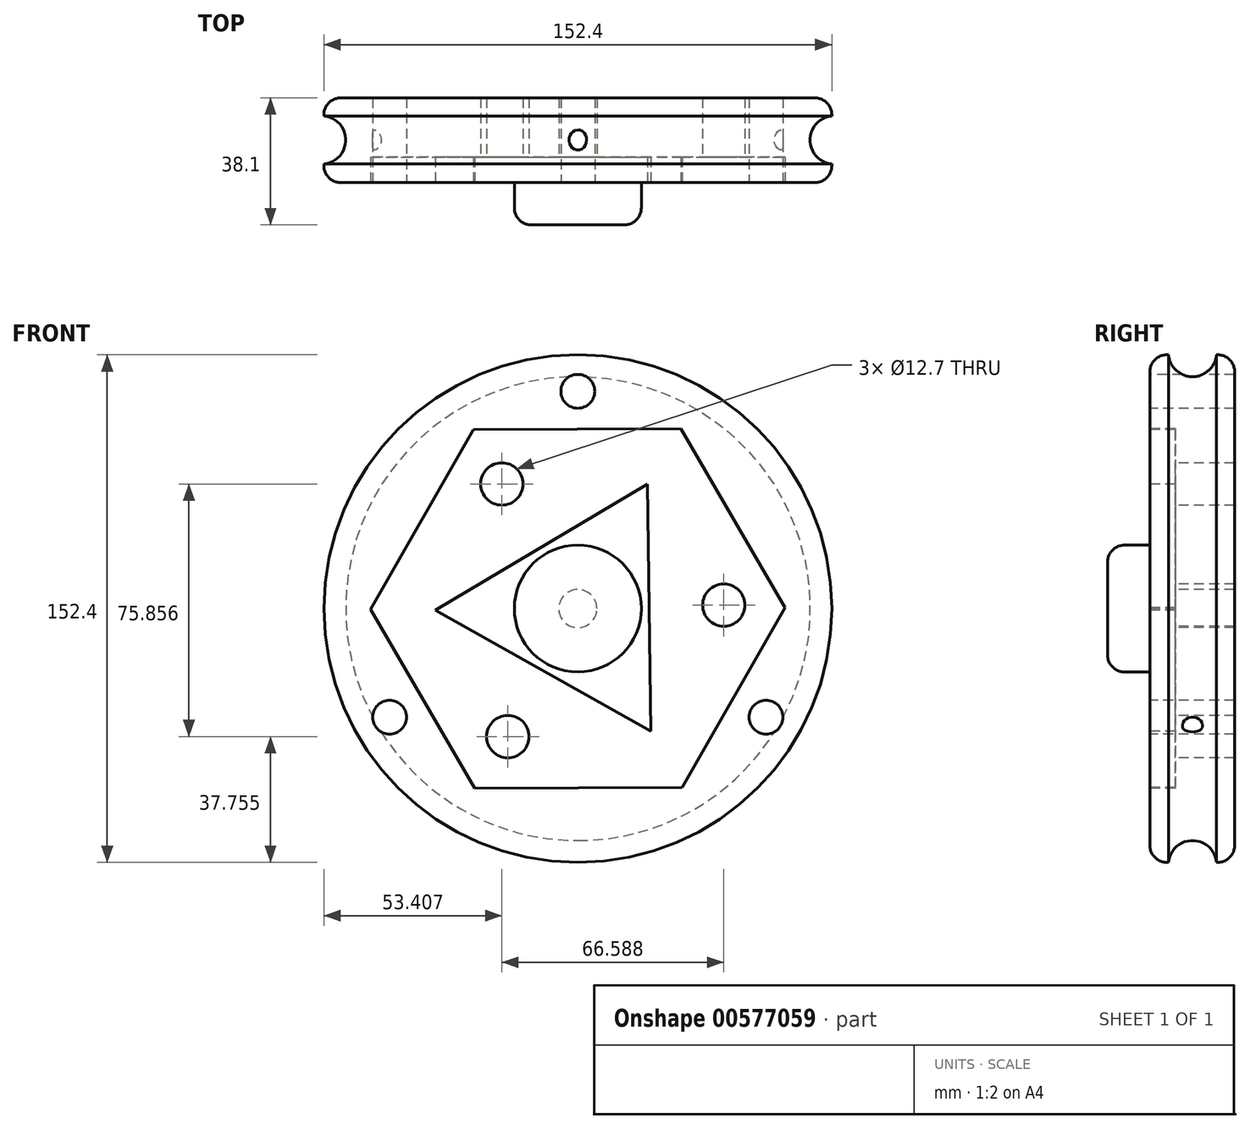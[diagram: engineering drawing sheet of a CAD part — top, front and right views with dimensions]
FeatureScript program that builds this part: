
annotation { "Feature Type Name" : "Feature", "Feature Type Description" : "" }
export const myFeature = defineFeature(function(context is Context, id is Id, definition is map)
    precondition{}
    {
        {
            var Q0;
            Q0=qCreatedBy(makeId("Front.planeOp"),FACE);
            var sketch = newSketch(context, id + "F0", { "sketchPlane" : qUnion([Q0])});
            skCircle(sketch, "E0", {"center": v(0, 0) * mm, "radius": 76.2 * mm});
            skSolve(sketch);
        }
        {
            var Q0;
            Q0=makeQuery(id+"F0.imprint","IMPRINT",FACE,{"disambiguationData":[TD([[makeQuery(id+"F0.imprint","IMPRINT",EDGE,{"derivedFrom":sQuery(id+"F0.wireOp",EDGE,"E0")}),1.0]])]});
            extrude(context, id + "F1", {"entities" : qUnion([Q0]), "depth" : 25.4 * mm, "offsetDistance" : 25.4 * mm});
        }
        {
            var Q0;
            Q0=makeQuery(id+"F1.opExtrude","CAP_FACE",FACE,{"disambiguationData":[OSD([sQuery(id+"F0.wireOp",EDGE,"E0")])],"isStart":false});
            var sketch = newSketch(context, id + "F2", { "sketchPlane" : qUnion([Q0])});
            skCircle(sketch, "E1", {"center": v(0, 0) * mm, "radius": 19.05 * mm});
            skSolve(sketch);
        }
        {
            var Q0;
            Q0=makeQuery(id+"F1.opExtrude","CAP_FACE",FACE,{"disambiguationData":[OSD([sQuery(id+"F0.wireOp",EDGE,"E0")])],"isStart":false});
            var sketch = newSketch(context, id + "F3", { "sketchPlane" : qUnion([Q0])});
            skSolve(sketch);
        }
        {
            var Q0;
            Q0=makeQuery(id+"F3.imprint","IMPRINT",FACE,{"disambiguationData":[TD([[makeQuery(id+"F3.imprint","IMPRINT",EDGE,{"derivedFrom":makeQuery(id+"F1.opExtrude","CAP_EDGE",EDGE,{"disambiguationData":[OSD([sQuery(id+"F0.wireOp",EDGE,"E0")])],"isStart":false})}),1.0]])]});
            var sketch = newSketch(context, id + "F4", { "sketchPlane" : qUnion([Q0])});
            skPoint(sketch, "E2", {"position": v(0, 0) * mm});
            skSolve(sketch);
        }
        {
            var Q0;
            Q0=sQuery(id+"F4.wireOp",VERTEX,"E2");
            var Q1;
            Q1=makeQuery(id+"F1.opExtrude","SWEPT_BODY",BODY,{"disambiguationData":[OSD([sQuery(id+"F0.wireOp",EDGE,"E0")])]});
            hole(context, id + "F5", {"style" : HoleStyle.SIMPLE, "endStyle" : HoleEndStyle.THROUGH, "holeDiameter" : 11.43 * mm, "isTappedThrough" : true, "tappedDepth" : 12.7 * mm, "tapClearance" : 3, "locations" : qUnion([Q0]), "scope" : qUnion([Q1])});
        }
        {
            var Q0;
            Q0=makeQuery(id+"F2.imprint","IMPRINT",FACE,{"disambiguationData":[TD([[makeQuery(id+"F2.imprint","IMPRINT",EDGE,{"derivedFrom":sQuery(id+"F2.wireOp",EDGE,"E1")}),1.0]])]});
            var sketch = newSketch(context, id + "F6", { "sketchPlane" : qUnion([Q0])});
            skCircle(sketch, "E3", {"center": v(0, 0) * mm, "radius": 19.05 * mm});
            skSolve(sketch);
        }
        {
            var Q0;
            Q0 = qSketchRegion(id + "F6", true);
            extrude(context, id + "F7", {"entities" : qUnion([Q0]), "operationType" : NewBodyOperationType.ADD, "depth" : 12.7 * mm, "offsetDistance" : 25.4 * mm});
        }
        {
            var Q0;
            Q0=makeQuery(id+"F1.opExtrude","SWEPT_FACE",FACE,{"disambiguationData":[OSD([sQuery(id+"F0.wireOp",EDGE,"E0")])]});
            var Q1;
            Q1=makeQuery(id+"F1.opExtrude","CAP_EDGE",EDGE,{"disambiguationData":[OSD([sQuery(id+"F0.wireOp",EDGE,"E0")])],"isStart":false});
            fillet(context, id + "F8", {"entities" : qUnion([Q0, Q1]), "radius" : 5.08 * mm, "tangentPropagation" : true, "allowEdgeOverflow" : false});
        }
        {
            var Q0;
            Q0=qCreatedBy(makeId("Right.planeOp"),FACE);
            var sketch = newSketch(context, id + "F9", { "sketchPlane" : qUnion([Q0])});
            skCircle(sketch, "E4", {"center": v(-12.62, 76.9) * mm, "radius": 7.25 * mm});
            skPoint(sketch, "E4.first.point", {"position": v(-19.88, 76.7) * mm});
            skPoint(sketch, "E4.second.point", {"position": v(-5.42, 76.03) * mm});
            skPoint(sketch, "E4.third.point", {"position": v(-10.02, 70.12) * mm});
            skSolve(sketch);
        }
        {
            var Q0;
            Q0=makeQuery(id+"F9.imprint","IMPRINT",FACE,{"disambiguationData":[TD([[makeQuery(id+"F9.imprint","IMPRINT",EDGE,{"derivedFrom":sQuery(id+"F9.wireOp",EDGE,"E4")}),1.0]])]});
            var Q1;
            {var subQ0=sQuery(id+"F0.wireOp",EDGE,"E0");Q1=makeQuery(id+"F8.opFillet","BLEND_EDGE",EDGE,{"blendedFrom":[makeQuery(id+"F1.opExtrude","CAP_EDGE",EDGE,{"disambiguationData":[OSD([subQ0])],"isStart":false}),makeQuery(id+"F1.opExtrude","CAP_FACE",FACE,{"disambiguationData":[OSD([subQ0])],"isStart":false})],"blendedInto":[makeQuery(id+"F1.opExtrude","CAP_FACE",FACE,{"disambiguationData":[OSD([subQ0])],"isStart":false})]});}
            revolve(context, id + "F10", {"operationType" : NewBodyOperationType.REMOVE, "entities" : qUnion([Q0]), "axis" : qUnion([Q1]), "revolveType" : RevolveType.FULL, "oppositeDirection" : true});
        }
        {
            var Q0;
            Q0=makeQuery(id+"F7.opExtrude","CAP_EDGE",EDGE,{"disambiguationData":[OSD([sQuery(id+"F6.wireOp",EDGE,"E3")])],"isStart":false});
            fillet(context, id + "F11", {"entities" : qUnion([Q0]), "radius" : 5.08 * mm, "tangentPropagation" : true, "allowEdgeOverflow" : false});
        }
        {
            var Q0;
            Q0=makeQuery(id+"F2.imprint","IMPRINT",FACE,{"disambiguationData":[TD([[makeQuery(id+"F2.imprint","IMPRINT",EDGE,{"derivedFrom":sQuery(id+"F2.wireOp",EDGE,"E1")}),-1.0]])]});
            var sketch = newSketch(context, id + "F12", { "sketchPlane" : qUnion([Q0])});
            skCircle(sketch, "E5.cCircle", {"center": v(0, 0) * mm, "radius": 62.2 * mm, "construction": true});
            skLineSegment(sketch, "E5.0", {"start": v(31.28, -53.76) * mm, "end": v(-30.92, -53.97) * mm});
            skLineSegment(sketch, "E5.1", {"start": v(-30.92, -53.97) * mm, "end": v(-62.2, -0.21) * mm});
            skLineSegment(sketch, "E5.2", {"start": v(-62.2, -0.21) * mm, "end": v(-31.28, 53.76) * mm});
            skLineSegment(sketch, "E5.3", {"start": v(-31.28, 53.76) * mm, "end": v(30.92, 53.97) * mm});
            skLineSegment(sketch, "E5.4", {"start": v(30.92, 53.97) * mm, "end": v(62.2, 0.21) * mm});
            skLineSegment(sketch, "E5.5", {"start": v(62.2, 0.21) * mm, "end": v(31.28, -53.76) * mm});
            skSolve(sketch);
        }
        {
            var Q0;
            Q0 = qSketchRegion(id + "F12", true);
            extrude(context, id + "F13", {"entities" : qUnion([Q0]), "operationType" : NewBodyOperationType.REMOVE, "oppositeDirection" : true, "depth" : 7.62 * mm, "offsetDistance" : 25.4 * mm});
        }
        {
            var Q0;
            Q0=makeQuery(id+"F2.imprint","IMPRINT",FACE,{"disambiguationData":[TD([[makeQuery(id+"F2.imprint","IMPRINT",EDGE,{"derivedFrom":sQuery(id+"F2.wireOp",EDGE,"E1")}),-1.0]])]});
            var sketch = newSketch(context, id + "F14", { "sketchPlane" : qUnion([Q0])});
            skCircle(sketch, "E6.cCircle", {"center": v(0, 0) * mm, "radius": 42.78 * mm, "construction": true});
            skLineSegment(sketch, "E6.0", {"start": v(21.85, -36.78) * mm, "end": v(-42.78, -0.53) * mm});
            skLineSegment(sketch, "E6.1", {"start": v(-42.78, -0.53) * mm, "end": v(20.93, 37.31) * mm});
            skLineSegment(sketch, "E6.2", {"start": v(20.93, 37.31) * mm, "end": v(21.85, -36.78) * mm});
            skSolve(sketch);
        }
        {
            var Q0;
            Q0 = qSketchRegion(id + "F14", true);
            extrude(context, id + "F15", {"entities" : qUnion([Q0]), "operationType" : NewBodyOperationType.ADD, "oppositeDirection" : true, "depth" : 7.62 * mm, "offsetDistance" : 25.4 * mm});
        }
        {
            var Q0;
            Q0=makeQuery(id+"F2.imprint","IMPRINT",FACE,{"disambiguationData":[TD([[makeQuery(id+"F2.imprint","IMPRINT",EDGE,{"derivedFrom":sQuery(id+"F2.wireOp",EDGE,"E1")}),-1.0]])]});
            var sketch = newSketch(context, id + "F16", { "sketchPlane" : qUnion([Q0])});
            skCircle(sketch, "E7", {"center": v(-22.8, 37.41) * mm, "radius": 6.35 * mm});
            skCircle(sketch, "E8.1.0", {"center": v(-21, -38.44) * mm, "radius": 6.35 * mm});
            skCircle(sketch, "E8.2.0", {"center": v(43.8, 1.03) * mm, "radius": 6.35 * mm});
            skPoint(sketch, "E8.center", {"position": v(0, 0) * mm});
            skSolve(sketch);
        }
        {
            var Q0;
            Q0 = qSketchRegion(id + "F16", true);
            extrude(context, id + "F17", {"entities" : qUnion([Q0]), "operationType" : NewBodyOperationType.REMOVE, "oppositeDirection" : true, "depth" : 25.4 * mm, "offsetDistance" : 25.4 * mm});
        }
        {
            var Q0;
            Q0=makeQuery(id+"F2.imprint","IMPRINT",FACE,{"disambiguationData":[TD([[makeQuery(id+"F2.imprint","IMPRINT",EDGE,{"derivedFrom":sQuery(id+"F2.wireOp",EDGE,"E1")}),-1.0]])]});
            var sketch = newSketch(context, id + "F18", { "sketchPlane" : qUnion([Q0])});
            skCircle(sketch, "E9", {"center": v(0, 65.22) * mm, "radius": 5.08 * mm});
            skCircle(sketch, "E10.1.0", {"center": v(-56.48, -32.61) * mm, "radius": 5.08 * mm});
            skCircle(sketch, "E10.2.0", {"center": v(56.48, -32.61) * mm, "radius": 5.08 * mm});
            skPoint(sketch, "E10.center", {"position": v(0, 0) * mm});
            skSolve(sketch);
        }
        {
            var Q0;
            Q0 = qSketchRegion(id + "F18", true);
            extrude(context, id + "F19", {"entities" : qUnion([Q0]), "operationType" : NewBodyOperationType.REMOVE, "oppositeDirection" : true, "depth" : 25.4 * mm, "offsetDistance" : 25.4 * mm});
        }
    });
